# Revit family: Legrand Colonnes universelles
name_source: partatom
category: Installations électriques
units: mm (PartAtom-declared; Revit-internal decimal feet)

## family parameters
Basée sur le plan de construction = Non
Conserver l'orientation des annotations = Non
Cote de connecteur circulaire = Utiliser le diamètre
Couper avec des vides une fois chargée = Non
Partagée = Non
Point de calcul de pièce = Non
Toujours verticalement = Oui
Type d'élément = Normal

## types (8) — shared parameters
Fabricant = LEGRAND
Largeur = 75 mm
Matériau principal = Aluminium
Standard = Universelle
Séparateur = 35 mm  [stored 0.114829 ft]
zero-valued in all types: Elévation par défaut

## per-type parameters (varying)
| type | 1 CPT | 2 CPT | Description | Finition | H1 | HC | Kit de finition perche | Longueur | Matériau couvercle | Matériaux corps | Modèle | Nombre de compartiments |
| Colonne 1cpt CV80 2,67m Blanc | Oui | Non | Colonne universelle 1 compartiment 2,67m Blanc | Blanc | 2700 mm | 2660 mm  [stored 8.72703 ft] | Kit de finition perche : Kit finition perche PVC Blanc | 82 mm | Legrand - Plastique blanc | Legrand - Aluminium blanc | LG-653110 | 1 compartiment |
| Colonne 1cpt CV80 2,67m Noir | Oui | Non | Colonne universelle 1 compartiment 2,67m Noir | Noir | 2700 mm | 2660 mm  [stored 8.72703 ft] | Kit de finition perche : Kit finition perche PVC Noir | 82 mm | Legrand - Plastique noir | Legrand - Aluminium noir | LG-653112 | 1 compartiment |
| Colonne 1cpt CV80 3,92m Blanc | Oui | Non | Colonne universelle 1 compartiment 3,92m Blanc | Blanc | 3900 mm  [stored 12.7953 ft] | 3860 mm  [stored 12.664 ft] | Kit de finition perche : Kit finition perche PVC Blanc | 82 mm | Legrand - Plastique blanc | Legrand - Aluminium blanc | LG-653113 | 1 compartiment |
| Colonne 1cpt CV80 3,92m Noir | Oui | Non | Colonne universelle 1 compartiment 3,92m Noir | Noir | 3900 mm  [stored 12.7953 ft] | 3860 mm  [stored 12.664 ft] | Kit de finition perche : Kit finition perche PVC Noir | 82 mm | Legrand - Plastique noir | Legrand - Aluminium noir | LG-653115 | 1 compartiment |
| Colonne 2 cpts CV80 2,67M Blanc | Non | Oui | Colonne universelle 2 compartiments 2,67m Blanc | Blanc | 2700 mm | 2660 mm  [stored 8.72703 ft] | Kit de finition perche : Kit finition perche PVC Blanc | 125 mm | Legrand - Plastique blanc | Legrand - Aluminium blanc | LG-653130 | 2 compartiments |
| Colonne 2 cpts CV80 2,67M Noir | Non | Oui | Colonne universelle 2 compartiments 2,67m Noir | Noir | 2700 mm | 2660 mm  [stored 8.72703 ft] | Kit de finition perche : Kit finition perche PVC Noir | 125 mm | Legrand - Plastique noir | Legrand - Aluminium noir | LG-653132 | 2 compartiments |
| Colonne 2 cpts CV80 3,92M Blanc | Non | Oui | Colonne universelle 2 compartiments 3,92m Blanc | Blanc | 3900 mm  [stored 12.7953 ft] | 3860 mm  [stored 12.664 ft] | Kit de finition perche : Kit finition perche PVC Blanc | 125 mm | Legrand - Plastique blanc | Legrand - Aluminium blanc | LG-653133 | 2 compartiments |
| Colonne 2 cpts CV80 3,92M Noir | Non | Oui | Colonne universelle 2 compartiments 3,92m Noir | Noir | 3900 mm  [stored 12.7953 ft] | 3860 mm  [stored 12.664 ft] | Kit de finition perche : Kit finition perche PVC Noir | 125 mm | Legrand - Plastique noir | Legrand - Aluminium noir | LG-653135 | 2 compartiments |

note: [stored X ft] marks values corroborated as IEEE doubles in the binary element streams (Revit-internal decimal feet)
